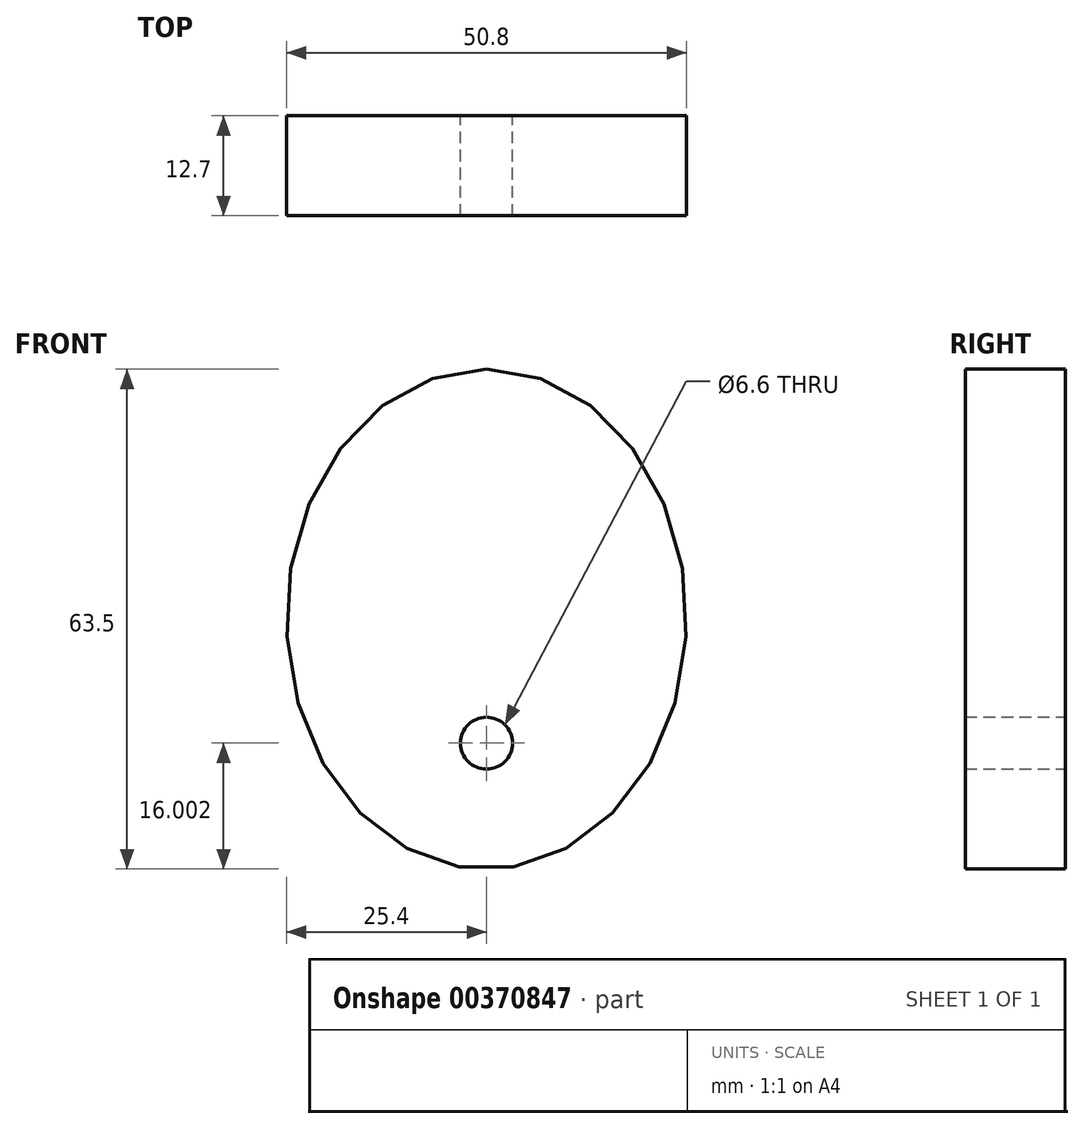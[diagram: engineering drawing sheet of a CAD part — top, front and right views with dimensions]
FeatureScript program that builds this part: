
annotation { "Feature Type Name" : "Feature", "Feature Type Description" : "" }
export const myFeature = defineFeature(function(context is Context, id is Id, definition is map)
    precondition{}
    {
        {
            var Q0;
            Q0=qCreatedBy(makeId("Front.planeOp"),FACE);
            var sketch = newSketch(context, id + "F0", { "sketchPlane" : qUnion([Q0])});
            skEllipse(sketch, "E0", {"center": v(0, 0) * mm, "majorRadius": 31.75 * mm, "minorRadius": 25.4 * mm, "majorAxis": v(0, 1)});
            skSolve(sketch);
        }
        {
            var Q0;
            Q0=makeQuery(id+"F0.imprint","IMPRINT",FACE,{"disambiguationData":[TD([[makeQuery(id+"F0.imprint","IMPRINT",EDGE,{"derivedFrom":sQuery(id+"F0.wireOp",EDGE,"E0")}),1.0]])]});
            extrude(context, id + "F1", {"entities" : qUnion([Q0]), "depth" : 12.7 * mm});
        }
        {
            var Q0;
            Q0=makeQuery(id+"F1.opExtrude","CAP_FACE",FACE,{"disambiguationData":[OSD([sQuery(id+"F0.wireOp",EDGE,"E0")])],"isStart":true});
            var sketch = newSketch(context, id + "F2", { "sketchPlane" : qUnion([Q0])});
            skCircle(sketch, "E1", {"center": v(0, -15.75) * mm, "radius": 3.3 * mm});
            skLineSegment(sketch, "E2", {"start": v(0, -15.75) * mm, "end": v(0, -31.75) * mm});
            skSolve(sketch);
        }
        {
            var Q0;
            Q0 = qSketchRegion(id + "F2", true);
            extrude(context, id + "F3", {"entities" : qUnion([Q0]), "operationType" : NewBodyOperationType.REMOVE, "oppositeDirection" : true, "depth" : 25.4 * mm});
        }
    });
